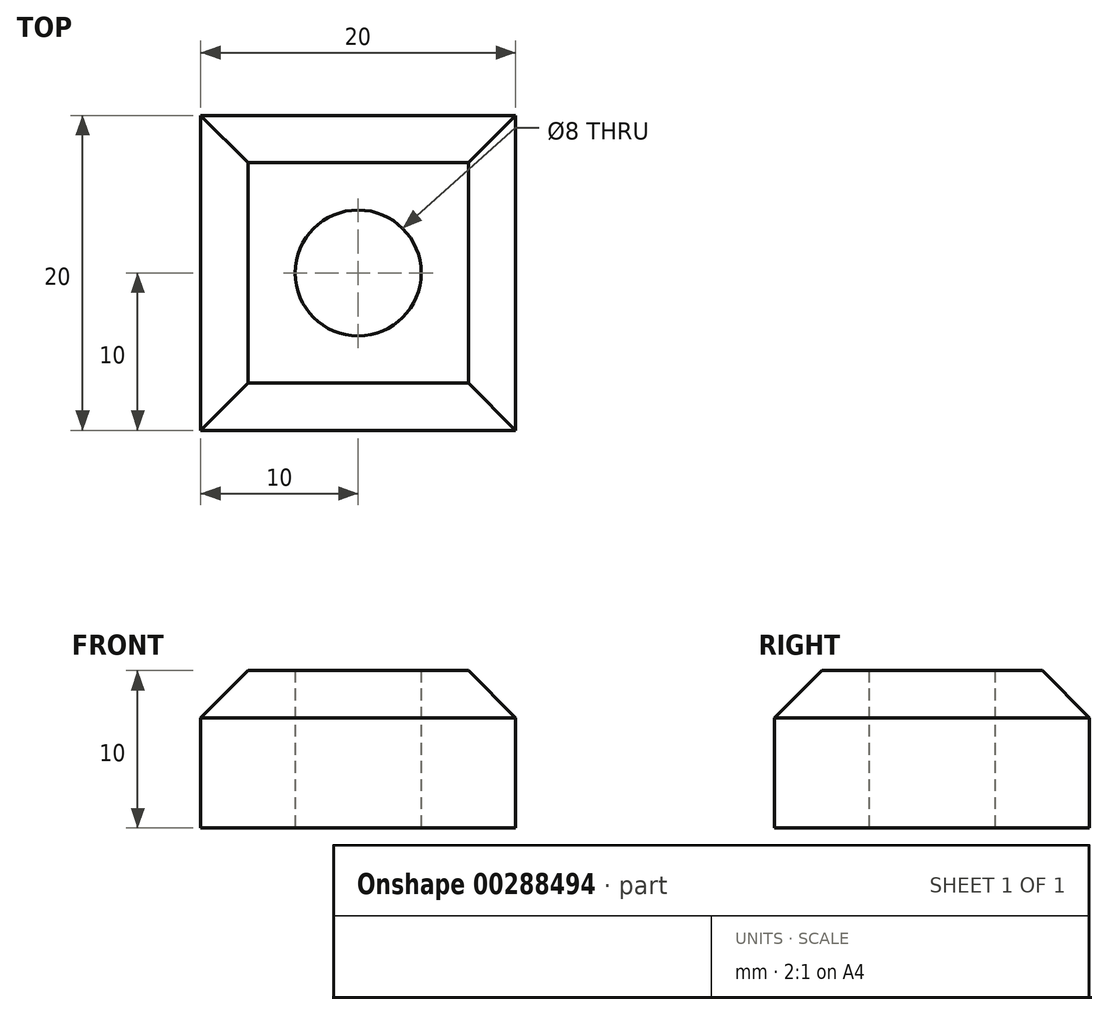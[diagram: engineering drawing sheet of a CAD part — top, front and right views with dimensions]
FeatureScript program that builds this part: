
annotation { "Feature Type Name" : "Feature", "Feature Type Description" : "" }
export const myFeature = defineFeature(function(context is Context, id is Id, definition is map)
    precondition{}
    {
        {
            var Q0;
            Q0=qCreatedBy(makeId("Top.planeOp"),FACE);
            var sketch = newSketch(context, id + "F0", { "sketchPlane" : qUnion([Q0])});
            skLineSegment(sketch, "E0.bottom", {"start": v(10, -10) * mm, "end": v(-10, -10) * mm});
            skLineSegment(sketch, "E0.top", {"start": v(10, 10) * mm, "end": v(-10, 10) * mm});
            skLineSegment(sketch, "E0.left", {"start": v(10, -10) * mm, "end": v(10, 10) * mm});
            skLineSegment(sketch, "E0.right", {"start": v(-10, -10) * mm, "end": v(-10, 10) * mm});
            skPoint(sketch, "E0.middle", {"position": v(0, 0) * mm});
            skCircle(sketch, "E1", {"center": v(0, 0) * mm, "radius": 4 * mm});
            skSolve(sketch);
        }
        {
            var Q0;
            Q0=makeQuery(id+"F0.imprint","IMPRINT",FACE,{"disambiguationData":[TD([[makeQuery(id+"F0.imprint","IMPRINT",EDGE,{"derivedFrom":sQuery(id+"F0.wireOp",EDGE,"E0.bottom")}),-1.0]])]});
            extrude(context, id + "F1", {"entities" : qUnion([Q0]), "depth" : 10 * mm});
        }
        {
            var Q0;
            Q0=makeQuery(id+"F1.opExtrude","CAP_EDGE",EDGE,{"disambiguationData":[OSD([sQuery(id+"F0.wireOp",EDGE,"E0.bottom")])],"isStart":false});
            var Q1;
            Q1=makeQuery(id+"F1.opExtrude","CAP_EDGE",EDGE,{"disambiguationData":[OSD([sQuery(id+"F0.wireOp",EDGE,"E0.right")])],"isStart":false});
            var Q2;
            Q2=makeQuery(id+"F1.opExtrude","CAP_EDGE",EDGE,{"disambiguationData":[OSD([sQuery(id+"F0.wireOp",EDGE,"E0.top")])],"isStart":false});
            var Q3;
            Q3=makeQuery(id+"F1.opExtrude","CAP_EDGE",EDGE,{"disambiguationData":[OSD([sQuery(id+"F0.wireOp",EDGE,"E0.left")])],"isStart":false});
            chamfer(context, id + "F2", {"entities" : qUnion([Q0, Q1, Q2, Q3]), "width" : 3 * mm, "tangentPropagation" : true});
        }
    });
